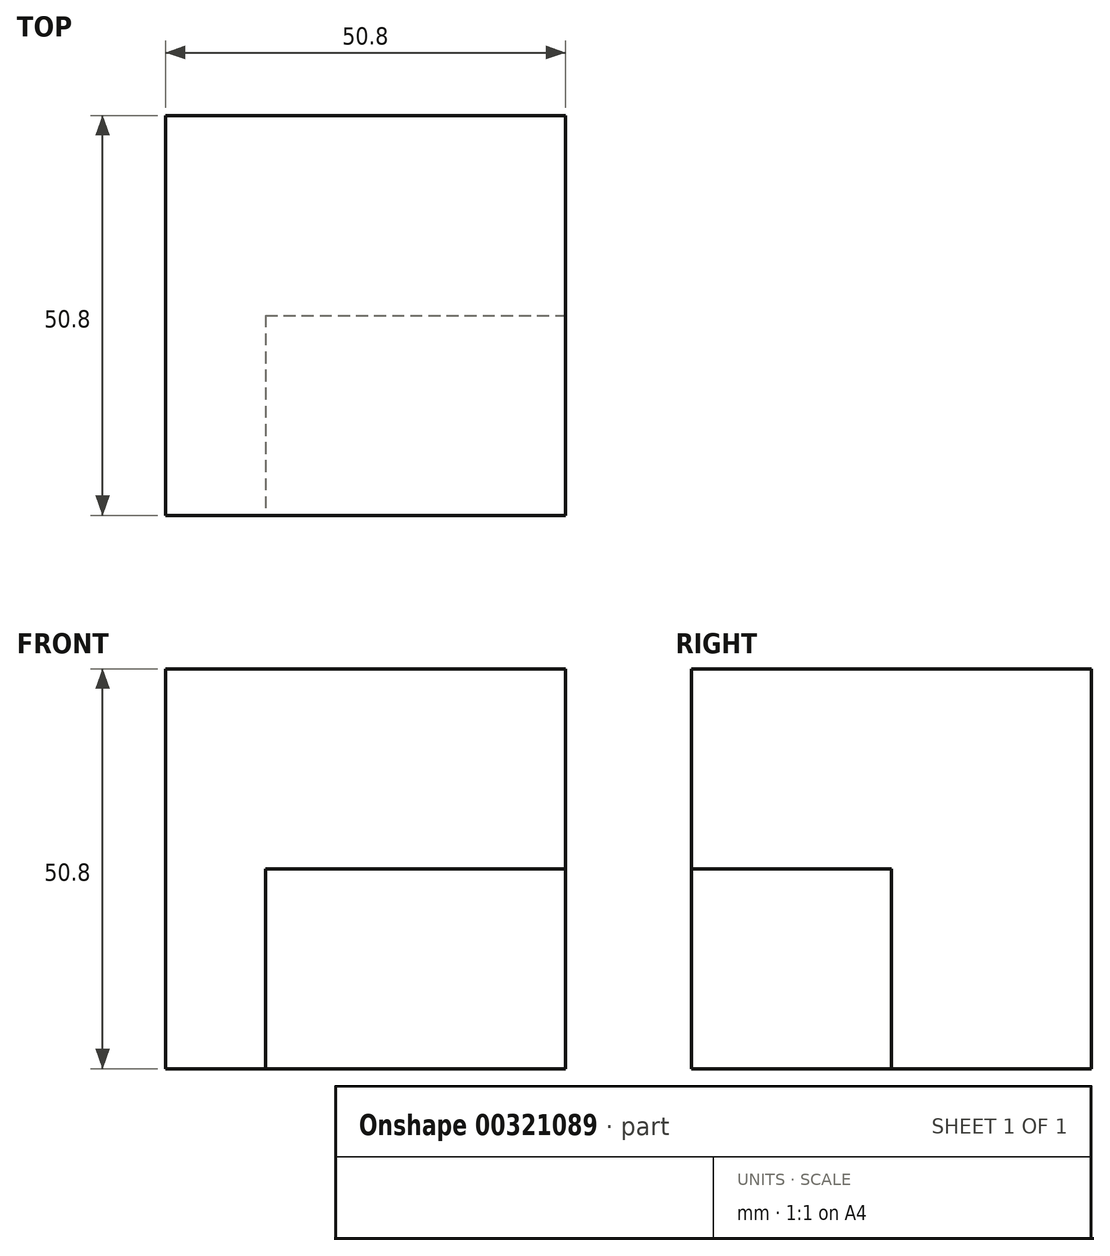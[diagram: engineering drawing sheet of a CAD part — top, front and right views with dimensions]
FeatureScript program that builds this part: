
annotation { "Feature Type Name" : "Feature", "Feature Type Description" : "" }
export const myFeature = defineFeature(function(context is Context, id is Id, definition is map)
    precondition{}
    {
        {
            var Q0;
            Q0=qCreatedBy(makeId("Top.planeOp"),FACE);
            var sketch = newSketch(context, id + "F0", { "sketchPlane" : qUnion([Q0])});
            skLineSegment(sketch, "E0", {"start": v(-21.75, 24.94) * mm, "end": v(-21.75, -25.86) * mm});
            skLineSegment(sketch, "E1", {"start": v(-21.75, -25.86) * mm, "end": v(29.05, -25.86) * mm});
            skLineSegment(sketch, "E2", {"start": v(29.05, -25.86) * mm, "end": v(29.05, 24.94) * mm});
            skLineSegment(sketch, "E3", {"start": v(29.05, 24.94) * mm, "end": v(-21.75, 24.94) * mm});
            skSolve(sketch);
        }
        {
            var Q0;
            Q0=makeQuery(id+"F0.imprint","IMPRINT",FACE,{"disambiguationData":[TD([[makeQuery(id+"F0.imprint","IMPRINT",EDGE,{"derivedFrom":sQuery(id+"F0.wireOp",EDGE,"E0")}),1.0]])]});
            extrude(context, id + "F1", {"entities" : qUnion([Q0]), "depth" : 50.8 * mm});
        }
        {
            var Q0;
            Q0=makeQuery(id+"F1.opExtrude","SWEPT_FACE",FACE,{"disambiguationData":[OSD([sQuery(id+"F0.wireOp",EDGE,"E1")])]});
            var sketch = newSketch(context, id + "F2", { "sketchPlane" : qUnion([Q0])});
            skLineSegment(sketch, "E4.bottom", {"start": v(29.05, 0) * mm, "end": v(-9.05, 0) * mm});
            skLineSegment(sketch, "E4.top", {"start": v(29.05, 25.4) * mm, "end": v(-9.05, 25.4) * mm});
            skLineSegment(sketch, "E4.left", {"start": v(29.05, 0) * mm, "end": v(29.05, 25.4) * mm});
            skLineSegment(sketch, "E4.right", {"start": v(-9.05, 0) * mm, "end": v(-9.05, 25.4) * mm});
            skSolve(sketch);
        }
        {
            var Q0;
            Q0 = qSketchRegion(id + "F2", true);
            var Q1;
            Q1=makeQuery(id+"F2.imprint","IMPRINT",FACE,{"disambiguationData":[TD([[makeQuery(id+"F2.imprint","IMPRINT",EDGE,{"derivedFrom":sQuery(id+"F2.wireOp",EDGE,"E4.bottom")}),1.0]])]});
            extrude(context, id + "F3", {"entities" : qUnion([Q0, Q1]), "operationType" : NewBodyOperationType.REMOVE, "oppositeDirection" : true, "depth" : 25.4 * mm});
        }
    });
